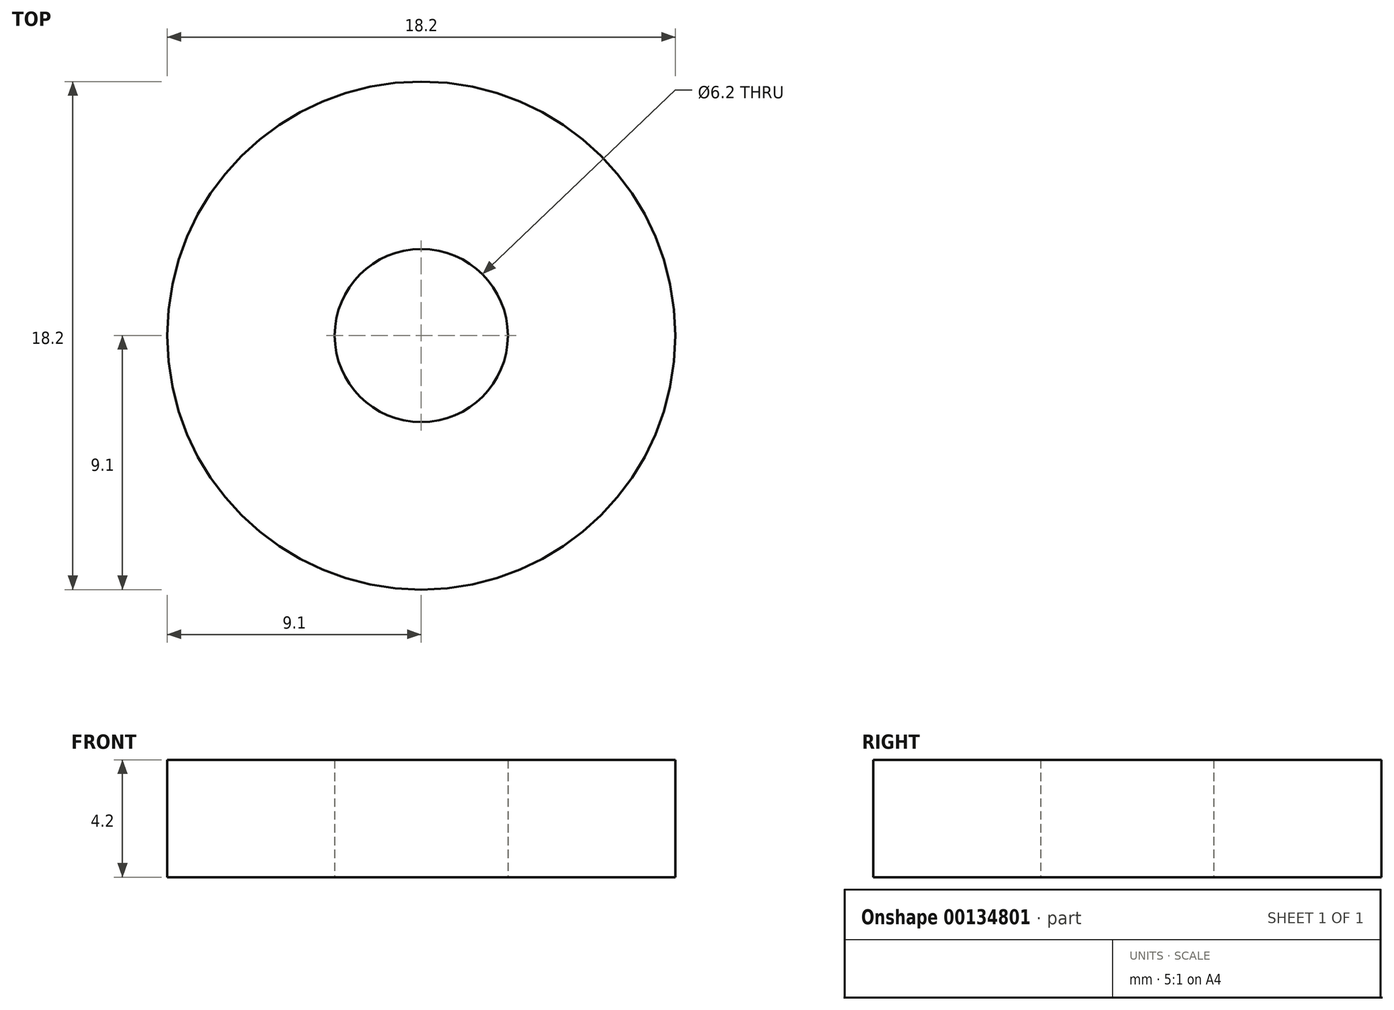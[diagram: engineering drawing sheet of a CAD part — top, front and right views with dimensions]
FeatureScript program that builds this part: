
annotation { "Feature Type Name" : "Feature", "Feature Type Description" : "" }
export const myFeature = defineFeature(function(context is Context, id is Id, definition is map)
    precondition{}
    {
        {
            var Q0;
            Q0=qCreatedBy(makeId("Top.planeOp"),FACE);
            var sketch = newSketch(context, id + "F0", { "sketchPlane" : qUnion([Q0])});
            skCircle(sketch, "E0", {"center": v(0, 0) * mm, "radius": 3.1 * mm});
            skCircle(sketch, "E1", {"center": v(0, 0) * mm, "radius": 9.1 * mm});
            skSolve(sketch);
        }
        {
            var Q0;
            Q0 = qSketchRegion(id + "F0", true);
            extrude(context, id + "F1", {"entities" : qUnion([Q0]), "depth" : 4.2 * mm});
        }
    });
